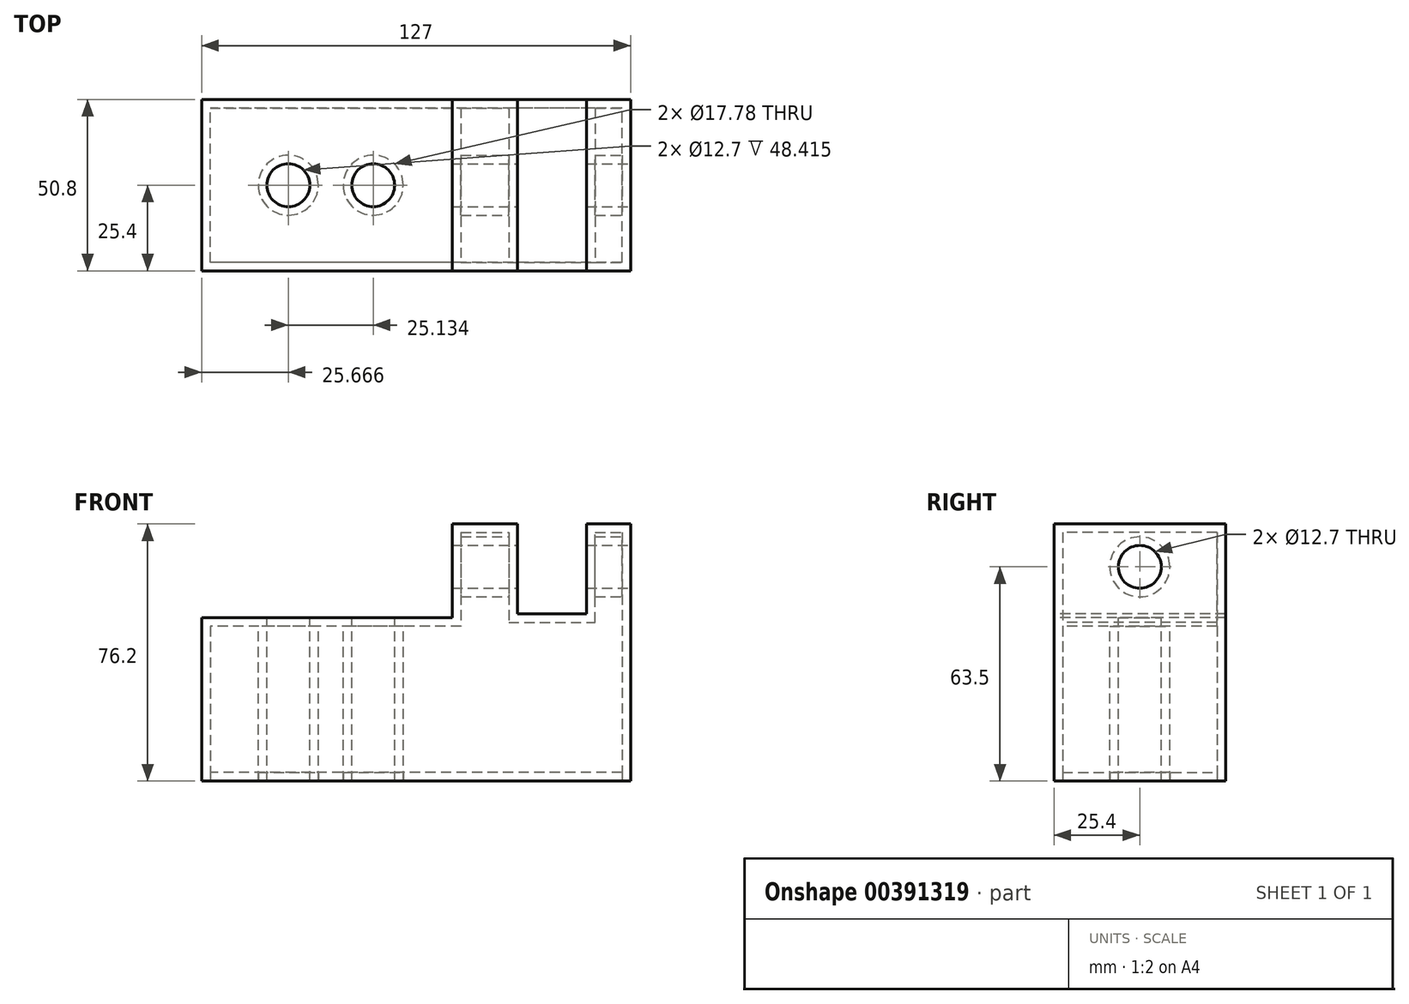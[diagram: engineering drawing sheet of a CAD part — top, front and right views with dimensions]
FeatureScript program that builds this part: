
annotation { "Feature Type Name" : "Feature", "Feature Type Description" : "" }
export const myFeature = defineFeature(function(context is Context, id is Id, definition is map)
    precondition{}
    {
        {
            var Q0;
            Q0=qCreatedBy(makeId("Front.planeOp"),FACE);
            var sketch = newSketch(context, id + "F0", { "sketchPlane" : qUnion([Q0])});
            skLineSegment(sketch, "E0", {"start": v(0, 76.2) * mm, "end": v(127, 76.2) * mm});
            skLineSegment(sketch, "E1", {"start": v(127, 76.2) * mm, "end": v(127, 0) * mm});
            skLineSegment(sketch, "E2", {"start": v(127, 0) * mm, "end": v(0, 0) * mm});
            skLineSegment(sketch, "E3", {"start": v(0, 76.2) * mm, "end": v(0, 0) * mm});
            skSolve(sketch);
        }
        {
            var Q0;
            Q0=makeQuery(id+"F0.imprint","IMPRINT",FACE,{"disambiguationData":[TD([[makeQuery(id+"F0.imprint","IMPRINT",EDGE,{"derivedFrom":sQuery(id+"F0.wireOp",EDGE,"E0")}),-1.0]])]});
            extrude(context, id + "F1", {"entities" : qUnion([Q0]), "depth" : 50.8 * mm});
        }
        {
            var Q0;
            Q0=makeQuery(id+"F1.opExtrude","CAP_FACE",FACE,{"disambiguationData":[OSD([sQuery(id+"F0.wireOp",EDGE,"E0"),sQuery(id+"F0.wireOp",EDGE,"E1"),sQuery(id+"F0.wireOp",EDGE,"E2"),sQuery(id+"F0.wireOp",EDGE,"E3")])],"isStart":false});
            var sketch = newSketch(context, id + "F2", { "sketchPlane" : qUnion([Q0])});
            skLineSegment(sketch, "E4", {"start": v(93.47, 76.2) * mm, "end": v(93.47, 49.6) * mm});
            skLineSegment(sketch, "E5", {"start": v(93.47, 49.6) * mm, "end": v(113.99, 49.6) * mm});
            skLineSegment(sketch, "E6", {"start": v(113.99, 49.6) * mm, "end": v(113.99, 76.2) * mm});
            skSolve(sketch);
        }
        {
            var Q0;
            {var subQ0=sQuery(id+"F2.wireOp",EDGE,"E4");Q0=makeQuery(id+"F2.imprint","IMPRINT",FACE,{"disambiguationData":[TD([[makeQuery(id+"F2.imprint","IMPRINT",EDGE,{"derivedFrom":subQ0}),1.0]])]});}
            extrude(context, id + "F3", {"entities" : qUnion([Q0]), "operationType" : NewBodyOperationType.REMOVE, "endBound" : BoundingType.UP_TO_NEXT, "oppositeDirection" : true, "depth" : 25.4 * mm});
        }
        {
            var Q0;
            {var subQ2=sQuery(id+"F2.wireOp",EDGE,"E4");Q0=makeQuery(id+"F2.imprint","IMPRINT",FACE,{"disambiguationData":[TD([[makeQuery(id+"F2.imprint","IMPRINT",EDGE,{"derivedFrom":subQ2}),-1.0]])]});}
            var sketch = newSketch(context, id + "F4", { "sketchPlane" : qUnion([Q0])});
            skLineSegment(sketch, "E7", {"start": v(74.23, 76.2) * mm, "end": v(74.23, 48.42) * mm});
            skLineSegment(sketch, "E8", {"start": v(74.23, 48.42) * mm, "end": v(0, 48.42) * mm});
            skLineSegment(sketch, "E9.0", {"start": v(0, 76.2) * mm, "end": v(93.47, 76.2) * mm});
            skPoint(sketch, "E10", {"position": v(74.23, 76.2) * mm});
            skPoint(sketch, "E11", {"position": v(0, 48.42) * mm});
            skSolve(sketch);
        }
        {
            var Q0;
            {var subQ0=sQuery(id+"F4.wireOp",EDGE,"E7");Q0=makeQuery(id+"F4.imprint","IMPRINT",FACE,{"disambiguationData":[TD([[makeQuery(id+"F4.imprint","IMPRINT",EDGE,{"derivedFrom":subQ0}),-1.0]])]});}
            extrude(context, id + "F5", {"entities" : qUnion([Q0]), "operationType" : NewBodyOperationType.REMOVE, "endBound" : BoundingType.UP_TO_NEXT, "oppositeDirection" : true, "depth" : 25.4 * mm});
        }
        {
            var Q0;
            Q0=makeQuery(id+"F1.opExtrude","SWEPT_FACE",FACE,{"disambiguationData":[OSD([sQuery(id+"F0.wireOp",EDGE,"E1")])]});
            var sketch = newSketch(context, id + "F6", { "sketchPlane" : qUnion([Q0])});
            skCircle(sketch, "E12", {"center": v(-25.4, 63.5) * mm, "radius": 6.35 * mm});
            skLineSegment(sketch, "E13.0", {"start": v(-50.8, 76.2) * mm, "end": v(0, 76.2) * mm});
            skSolve(sketch);
        }
        {
            var Q0;
            Q0=makeQuery(id+"F6.imprint","IMPRINT",FACE,{"disambiguationData":[TD([[makeQuery(id+"F6.imprint","IMPRINT",EDGE,{"derivedFrom":sQuery(id+"F6.wireOp",EDGE,"E12")}),1.0]])]});
            var Q1;
            Q1=makeQuery(id+"F5.boolean.opBoolean","COPY",FACE,{"derivedFrom":makeQuery(id+"F5.opExtrude","SWEPT_FACE",FACE,{"disambiguationData":[OSD([sQuery(id+"F4.wireOp",EDGE,"E7")])]})});
            extrude(context, id + "F7", {"entities" : qUnion([Q0]), "operationType" : NewBodyOperationType.REMOVE, "endBound" : BoundingType.THROUGH_ALL, "oppositeDirection" : true, "endBoundEntityFace" : qUnion([Q1]), "depth" : 25.4 * mm});
        }
        {
            var Q0;
            Q0=makeQuery(id+"F5.boolean.opBoolean","COPY",FACE,{"derivedFrom":makeQuery(id+"F5.opExtrude","SWEPT_FACE",FACE,{"disambiguationData":[OSD([sQuery(id+"F4.wireOp",EDGE,"E8")])]})});
            var sketch = newSketch(context, id + "F8", { "sketchPlane" : qUnion([Q0])});
            skCircle(sketch, "E14", {"center": v(50.8, -25.4) * mm, "radius": 6.35 * mm});
            skSolve(sketch);
        }
        {
            var Q0;
            Q0=qSketchRegion(id+"F8",true);
            extrude(context, id + "F9", {"entities" : qUnion([Q0]), "operationType" : NewBodyOperationType.REMOVE, "endBound" : BoundingType.UP_TO_NEXT, "oppositeDirection" : true, "depth" : 25.4 * mm});
        }
        {
            var Q0;
            Q0=makeQuery(id+"F5.boolean.opBoolean","COPY",FACE,{"derivedFrom":makeQuery(id+"F5.opExtrude","SWEPT_FACE",FACE,{"disambiguationData":[OSD([sQuery(id+"F4.wireOp",EDGE,"E8")])]})});
            var sketch = newSketch(context, id + "F10", { "sketchPlane" : qUnion([Q0])});
            skCircle(sketch, "E15", {"center": v(25.67, -25.4) * mm, "radius": 6.35 * mm});
            skSolve(sketch);
        }
        {
            var Q0;
            Q0=makeQuery(id+"F10.imprint","IMPRINT",FACE,{"disambiguationData":[TD([[makeQuery(id+"F10.imprint","IMPRINT",EDGE,{"derivedFrom":sQuery(id+"F10.wireOp",EDGE,"E15")}),1.0]])]});
            extrude(context, id + "F11", {"entities" : qUnion([Q0]), "operationType" : NewBodyOperationType.REMOVE, "endBound" : BoundingType.UP_TO_NEXT, "oppositeDirection" : true, "depth" : 25.4 * mm});
        }
        {
            var Q0;
            Q0=makeQuery(id+"F1.opExtrude","SWEPT_FACE",FACE,{"disambiguationData":[OSD([sQuery(id+"F0.wireOp",EDGE,"E2")])]});
            cPlane(context, id + "F12", {"entities" : qUnion([Q0]), "cplaneType" : CPlaneType.OFFSET, "offset" : 0 * mm, "width" : 152.4 * mm, "height" : 152.4 * mm});
        }
        {
            var Q0;
            Q0=makeQuery(id+"F1.opExtrude","SWEPT_FACE",FACE,{"disambiguationData":[OSD([sQuery(id+"F0.wireOp",EDGE,"E2")])]});
            shell(context, id + "F13", {"entities" : qUnion([Q0]), "thickness" : 2.54 * mm});
        }
        {
            var Q0;
            Q0=qCreatedBy(id+"F12.planeOp",FACE);
            var sketch = newSketch(context, id + "F14", { "sketchPlane" : qUnion([Q0])});
            skCircle(sketch, "E16.0", {"center": v(50.8, 25.4) * mm, "radius": 8.9 * mm});
            skCircle(sketch, "E17.0", {"center": v(25.67, 25.4) * mm, "radius": 8.9 * mm});
            skLineSegment(sketch, "E18.0", {"start": v(124.46, 48.26) * mm, "end": v(2.54, 48.26) * mm});
            skLineSegment(sketch, "E19.0", {"start": v(124.46, 48.26) * mm, "end": v(124.46, 2.54) * mm});
            skLineSegment(sketch, "E20.0", {"start": v(124.46, 2.54) * mm, "end": v(2.54, 2.54) * mm});
            skLineSegment(sketch, "E21.0", {"start": v(2.54, 48.26) * mm, "end": v(2.54, 2.54) * mm});
            skSolve(sketch);
        }
        {
            var Q0;
            Q0=qSketchRegion(id+"F14",true);
            extrude(context, id + "F15", {"entities" : qUnion([Q0]), "oppositeDirection" : true, "depth" : 2.54 * mm});
        }
    });
